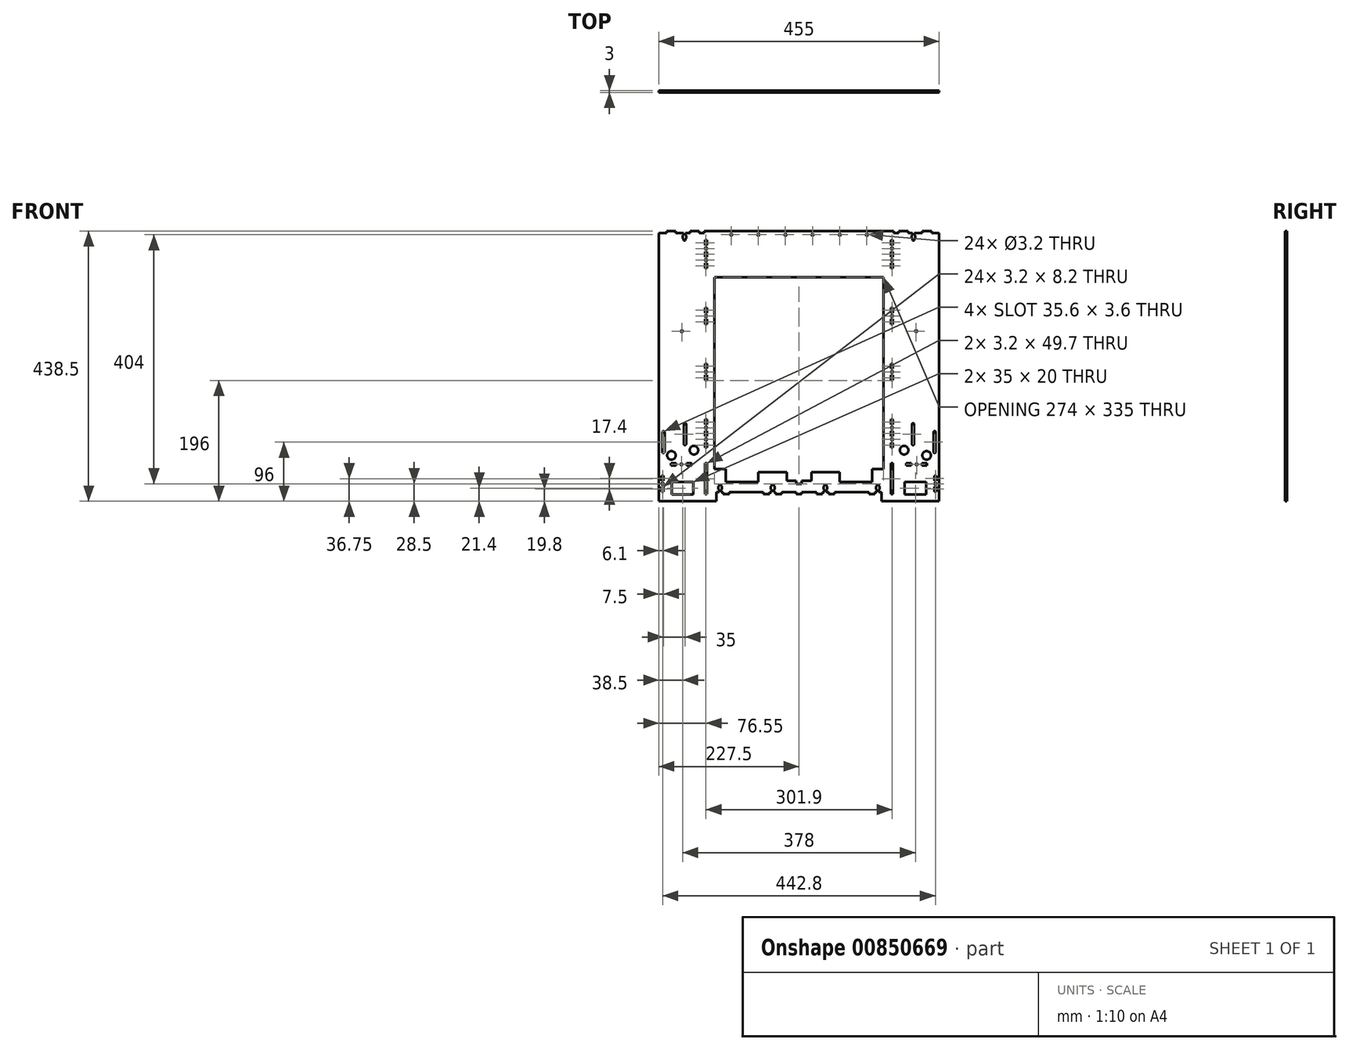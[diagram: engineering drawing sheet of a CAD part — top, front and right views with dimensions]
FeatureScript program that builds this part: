
annotation { "Feature Type Name" : "Feature", "Feature Type Description" : "" }
export const myFeature = defineFeature(function(context is Context, id is Id, definition is map)
    precondition{}
    {
        {
            var Q0;
            Q0=qCreatedBy(makeId("Front.planeOp"),FACE);
            var sketch = newSketch(context, id + "F0", { "sketchPlane" : qUnion([Q0])});
            skLineSegment(sketch, "E0", {"start": v(0, 0) * mm, "end": v(0, 435.5) * mm});
            skLineSegment(sketch, "E1", {"start": v(0, 435.5) * mm, "end": v(12.5, 435.5) * mm});
            skLineSegment(sketch, "E2", {"start": v(12.5, 435.5) * mm, "end": v(12.5, 438.5) * mm});
            skLineSegment(sketch, "E3", {"start": v(12.5, 438.5) * mm, "end": v(27.5, 438.5) * mm});
            skLineSegment(sketch, "E4", {"start": v(27.5, 438.5) * mm, "end": v(27.5, 435.5) * mm});
            skLineSegment(sketch, "E5", {"start": v(27.5, 435.5) * mm, "end": v(40, 435.5) * mm});
            skLineSegment(sketch, "E6", {"start": v(40, 435.5) * mm, "end": v(40, 431.2) * mm});
            skLineSegment(sketch, "E7", {"start": v(40, 431.2) * mm, "end": v(38.75, 431.2) * mm});
            skLineSegment(sketch, "E8", {"start": v(38.75, 431.2) * mm, "end": v(38.75, 426.2) * mm});
            skLineSegment(sketch, "E9", {"start": v(38.75, 426.2) * mm, "end": v(40, 426.2) * mm});
            skLineSegment(sketch, "E10", {"start": v(40, 426.2) * mm, "end": v(40, 423.5) * mm});
            skLineSegment(sketch, "E11", {"start": v(40, 423.5) * mm, "end": v(43.5, 423.5) * mm});
            skLineSegment(sketch, "E12", {"start": v(43.5, 423.5) * mm, "end": v(43.5, 426.2) * mm});
            skLineSegment(sketch, "E13", {"start": v(43.5, 426.2) * mm, "end": v(44.75, 426.2) * mm});
            skLineSegment(sketch, "E14", {"start": v(44.75, 426.2) * mm, "end": v(44.75, 431.2) * mm});
            skLineSegment(sketch, "E15", {"start": v(44.75, 431.2) * mm, "end": v(43.5, 431.2) * mm});
            skLineSegment(sketch, "E16", {"start": v(43.5, 431.2) * mm, "end": v(43.5, 435.5) * mm});
            skLineSegment(sketch, "E17", {"start": v(43.5, 435.5) * mm, "end": v(50.7, 435.5) * mm});
            skLineSegment(sketch, "E18", {"start": v(50.7, 435.5) * mm, "end": v(50.7, 438.5) * mm});
            skLineSegment(sketch, "E19", {"start": v(50.7, 438.5) * mm, "end": v(65.7, 438.5) * mm});
            skLineSegment(sketch, "E20", {"start": v(65.7, 438.5) * mm, "end": v(65.7, 435.5) * mm});
            skLineSegment(sketch, "E21", {"start": v(65.7, 435.5) * mm, "end": v(73.9, 435.5) * mm});
            skLineSegment(sketch, "E22", {"start": v(73.9, 435.5) * mm, "end": v(73.9, 438.5) * mm});
            skLineSegment(sketch, "E23", {"start": v(73.9, 438.5) * mm, "end": v(227.5, 438.5) * mm});
            skLineSegment(sketch, "E24", {"start": v(0, 0) * mm, "end": v(93.35, 0) * mm});
            skLineSegment(sketch, "E25", {"start": v(93.35, 0) * mm, "end": v(93.35, 15) * mm});
            skLineSegment(sketch, "E26", {"start": v(93.35, 15) * mm, "end": v(97.75, 15) * mm});
            skLineSegment(sketch, "E27", {"start": v(97.75, 15) * mm, "end": v(97.75, 19.3) * mm});
            skLineSegment(sketch, "E28", {"start": v(97.75, 19.3) * mm, "end": v(96.5, 19.3) * mm});
            skLineSegment(sketch, "E29", {"start": v(96.5, 19.3) * mm, "end": v(96.5, 24.3) * mm});
            skLineSegment(sketch, "E30", {"start": v(96.5, 24.3) * mm, "end": v(97.75, 24.3) * mm});
            skLineSegment(sketch, "E31", {"start": v(97.75, 24.3) * mm, "end": v(97.75, 27) * mm});
            skLineSegment(sketch, "E32", {"start": v(97.75, 27) * mm, "end": v(101.25, 27) * mm});
            skLineSegment(sketch, "E33", {"start": v(101.25, 27) * mm, "end": v(101.25, 24.3) * mm});
            skLineSegment(sketch, "E34", {"start": v(101.25, 24.3) * mm, "end": v(102.5, 24.3) * mm});
            skLineSegment(sketch, "E35", {"start": v(102.5, 24.3) * mm, "end": v(102.5, 19.3) * mm});
            skLineSegment(sketch, "E36", {"start": v(102.5, 19.3) * mm, "end": v(101.25, 19.3) * mm});
            skLineSegment(sketch, "E37", {"start": v(101.25, 19.3) * mm, "end": v(101.25, 15) * mm});
            skLineSegment(sketch, "E38", {"start": v(101.25, 15) * mm, "end": v(104.35, 15) * mm});
            skLineSegment(sketch, "E39", {"start": v(104.35, 15) * mm, "end": v(104.35, 12) * mm});
            skLineSegment(sketch, "E40", {"start": v(104.35, 12) * mm, "end": v(114.15, 12) * mm});
            skLineSegment(sketch, "E41", {"start": v(114.15, 12) * mm, "end": v(114.15, 15) * mm});
            skLineSegment(sketch, "E42", {"start": v(114.15, 15) * mm, "end": v(169.85, 15) * mm});
            skLineSegment(sketch, "E43", {"start": v(169.85, 15) * mm, "end": v(169.85, 12) * mm});
            skLineSegment(sketch, "E44", {"start": v(169.85, 12) * mm, "end": v(179.65, 12) * mm});
            skLineSegment(sketch, "E45", {"start": v(179.65, 12) * mm, "end": v(179.65, 15) * mm});
            skLineSegment(sketch, "E46", {"start": v(179.65, 15) * mm, "end": v(183.05, 15) * mm});
            skLineSegment(sketch, "E47", {"start": v(183.05, 15) * mm, "end": v(183.05, 19.3) * mm});
            skLineSegment(sketch, "E48", {"start": v(183.05, 19.3) * mm, "end": v(181.8, 19.3) * mm});
            skLineSegment(sketch, "E49", {"start": v(181.8, 19.3) * mm, "end": v(181.8, 24.3) * mm});
            skLineSegment(sketch, "E50", {"start": v(181.8, 24.3) * mm, "end": v(183.05, 24.3) * mm});
            skLineSegment(sketch, "E51", {"start": v(183.05, 24.3) * mm, "end": v(183.05, 27) * mm});
            skLineSegment(sketch, "E52", {"start": v(183.05, 27) * mm, "end": v(186.55, 27) * mm});
            skLineSegment(sketch, "E53", {"start": v(186.55, 27) * mm, "end": v(186.55, 24.3) * mm});
            skLineSegment(sketch, "E54", {"start": v(186.55, 24.3) * mm, "end": v(187.8, 24.3) * mm});
            skLineSegment(sketch, "E55", {"start": v(187.8, 24.3) * mm, "end": v(187.8, 19.3) * mm});
            skLineSegment(sketch, "E56", {"start": v(187.8, 19.3) * mm, "end": v(186.55, 19.3) * mm});
            skLineSegment(sketch, "E57", {"start": v(186.55, 19.3) * mm, "end": v(186.55, 15) * mm});
            skLineSegment(sketch, "E58", {"start": v(186.55, 15) * mm, "end": v(189.35, 15) * mm});
            skLineSegment(sketch, "E59", {"start": v(189.35, 15) * mm, "end": v(189.35, 12) * mm});
            skLineSegment(sketch, "E60", {"start": v(189.35, 12) * mm, "end": v(199.15, 12) * mm});
            skLineSegment(sketch, "E61", {"start": v(199.15, 12) * mm, "end": v(199.15, 15) * mm});
            skLineSegment(sketch, "E62", {"start": v(199.15, 15) * mm, "end": v(223, 15) * mm});
            skLineSegment(sketch, "E63", {"start": v(223, 15) * mm, "end": v(223, 12) * mm});
            skLineSegment(sketch, "E64", {"start": v(223, 12) * mm, "end": v(227.5, 12) * mm});
            skLineSegment(sketch, "E65", {"start": v(227.5, 12) * mm, "end": v(227.5, 438.5) * mm, "construction": true});
            skLineSegment(sketch, "E66", {"start": v(227.5, 28.5) * mm, "end": v(223, 28.5) * mm});
            skLineSegment(sketch, "E67", {"start": v(223, 28.5) * mm, "end": v(223, 33.5) * mm});
            skLineSegment(sketch, "E68", {"start": v(223, 33.5) * mm, "end": v(207.5, 33.5) * mm});
            skLineSegment(sketch, "E69", {"start": v(207.5, 33.5) * mm, "end": v(207.5, 47.5) * mm});
            skLineSegment(sketch, "E70", {"start": v(207.5, 47.5) * mm, "end": v(161.5, 47.5) * mm});
            skLineSegment(sketch, "E71", {"start": v(161.5, 47.5) * mm, "end": v(161.5, 31.5) * mm});
            skLineSegment(sketch, "E72", {"start": v(161.5, 31.5) * mm, "end": v(108.6, 31.5) * mm});
            skLineSegment(sketch, "E73", {"start": v(108.6, 31.5) * mm, "end": v(108.6, 52.5) * mm});
            skLineSegment(sketch, "E74", {"start": v(227.5, 363.5) * mm, "end": v(90.5, 363.5) * mm});
            skLineSegment(sketch, "E75", {"start": v(108.6, 52.5) * mm, "end": v(90.5, 52.5) * mm});
            skLineSegment(sketch, "E76", {"start": v(90.5, 363.5) * mm, "end": v(90.5, 52.5) * mm});
            skCircle(sketch, "E77", {"center": v(117.5, 432.5) * mm, "radius": 1.6 * mm});
            skCircle(sketch, "E78.1.0.0", {"center": v(161.5, 432.5) * mm, "radius": 1.6 * mm});
            skCircle(sketch, "E78.2.0.0", {"center": v(205.5, 432.5) * mm, "radius": 1.6 * mm});
            skLineSegment(sketch, "E78.direction1", {"start": v(117.5, 432.5) * mm, "end": v(161.5, 432.5) * mm, "construction": true});
            skLineSegment(sketch, "E79.MirrorCS", {"start": v(268.45, 24.3) * mm, "end": v(267.2, 24.3) * mm});
            skLineSegment(sketch, "E80.MirrorCS", {"start": v(411.5, 423.5) * mm, "end": v(411.5, 426.2) * mm});
            skLineSegment(sketch, "E81.MirrorCS", {"start": v(353.75, 24.3) * mm, "end": v(352.5, 24.3) * mm});
            skLineSegment(sketch, "E82.MirrorCS", {"start": v(271.95, 24.3) * mm, "end": v(271.95, 27) * mm});
            skLineSegment(sketch, "E83.MirrorCS", {"start": v(275.35, 15) * mm, "end": v(271.95, 15) * mm});
            skLineSegment(sketch, "E84.MirrorCS", {"start": v(353.75, 15) * mm, "end": v(350.65, 15) * mm});
            skLineSegment(sketch, "E85.MirrorCS", {"start": v(410.25, 431.2) * mm, "end": v(411.5, 431.2) * mm});
            skLineSegment(sketch, "E86.MirrorCS", {"start": v(411.5, 426.2) * mm, "end": v(410.25, 426.2) * mm});
            skLineSegment(sketch, "E87.MirrorCS", {"start": v(352.5, 19.3) * mm, "end": v(353.75, 19.3) * mm});
            skLineSegment(sketch, "E88.MirrorCS", {"start": v(357.25, 24.3) * mm, "end": v(357.25, 27) * mm});
            skLineSegment(sketch, "E89.MirrorCS", {"start": v(273.2, 24.3) * mm, "end": v(271.95, 24.3) * mm});
            skLineSegment(sketch, "E90.MirrorCS", {"start": v(353.75, 27) * mm, "end": v(353.75, 24.3) * mm});
            skLineSegment(sketch, "E91.MirrorCS", {"start": v(268.45, 27) * mm, "end": v(268.45, 24.3) * mm});
            skLineSegment(sketch, "E92.MirrorCS", {"start": v(415, 426.2) * mm, "end": v(415, 423.5) * mm});
            skLineSegment(sketch, "E93.MirrorCS", {"start": v(358.5, 24.3) * mm, "end": v(357.25, 24.3) * mm});
            skLineSegment(sketch, "E94.MirrorCS", {"start": v(267.2, 19.3) * mm, "end": v(268.45, 19.3) * mm});
            skLineSegment(sketch, "E95.MirrorCS", {"start": v(357.25, 19.3) * mm, "end": v(358.5, 19.3) * mm});
            skLineSegment(sketch, "E96.MirrorCS", {"start": v(410.25, 426.2) * mm, "end": v(410.25, 431.2) * mm});
            skLineSegment(sketch, "E97.MirrorCS", {"start": v(273.2, 19.3) * mm, "end": v(273.2, 24.3) * mm});
            skLineSegment(sketch, "E98.MirrorCS", {"start": v(268.45, 15) * mm, "end": v(265.65, 15) * mm});
            skLineSegment(sketch, "E99.MirrorCS", {"start": v(271.95, 27) * mm, "end": v(268.45, 27) * mm});
            skLineSegment(sketch, "E100.MirrorCS", {"start": v(415, 435.5) * mm, "end": v(415, 431.2) * mm});
            skLineSegment(sketch, "E101.MirrorCS", {"start": v(265.65, 15) * mm, "end": v(265.65, 12) * mm});
            skLineSegment(sketch, "E102.MirrorCS", {"start": v(267.2, 24.3) * mm, "end": v(267.2, 19.3) * mm});
            skLineSegment(sketch, "E103.MirrorCS", {"start": v(271.95, 15) * mm, "end": v(271.95, 19.3) * mm});
            skLineSegment(sketch, "E104.MirrorCS", {"start": v(415, 431.2) * mm, "end": v(416.25, 431.2) * mm});
            skLineSegment(sketch, "E105.MirrorCS", {"start": v(404.3, 435.5) * mm, "end": v(404.3, 438.5) * mm});
            skLineSegment(sketch, "E106.MirrorCS", {"start": v(416.25, 431.2) * mm, "end": v(416.25, 426.2) * mm});
            skLineSegment(sketch, "E107.MirrorCS", {"start": v(350.65, 15) * mm, "end": v(350.65, 12) * mm});
            skLineSegment(sketch, "E108.MirrorCS", {"start": v(268.45, 19.3) * mm, "end": v(268.45, 15) * mm});
            skLineSegment(sketch, "E109.MirrorCS", {"start": v(271.95, 19.3) * mm, "end": v(273.2, 19.3) * mm});
            skLineSegment(sketch, "E110.MirrorCS", {"start": v(411.5, 435.5) * mm, "end": v(404.3, 435.5) * mm});
            skLineSegment(sketch, "E111.MirrorCS", {"start": v(361.65, 15) * mm, "end": v(357.25, 15) * mm});
            skLineSegment(sketch, "E112.MirrorCS", {"start": v(416.25, 426.2) * mm, "end": v(415, 426.2) * mm});
            skLineSegment(sketch, "E113.MirrorCS", {"start": v(427.5, 435.5) * mm, "end": v(415, 435.5) * mm});
            skLineSegment(sketch, "E114.MirrorCS", {"start": v(353.75, 19.3) * mm, "end": v(353.75, 15) * mm});
            skLineSegment(sketch, "E115.MirrorCS", {"start": v(357.25, 15) * mm, "end": v(357.25, 19.3) * mm});
            skLineSegment(sketch, "E116.MirrorCS", {"start": v(358.5, 19.3) * mm, "end": v(358.5, 24.3) * mm});
            skLineSegment(sketch, "E117.MirrorCS", {"start": v(415, 423.5) * mm, "end": v(411.5, 423.5) * mm});
            skLineSegment(sketch, "E118.MirrorCS", {"start": v(357.25, 27) * mm, "end": v(353.75, 27) * mm});
            skLineSegment(sketch, "E119.MirrorCS", {"start": v(352.5, 24.3) * mm, "end": v(352.5, 19.3) * mm});
            skLineSegment(sketch, "E120.MirrorCS", {"start": v(275.35, 12) * mm, "end": v(275.35, 15) * mm});
            skLineSegment(sketch, "E121.MirrorCS", {"start": v(411.5, 431.2) * mm, "end": v(411.5, 435.5) * mm});
            skLineSegment(sketch, "E122.MirrorCS", {"start": v(265.65, 12) * mm, "end": v(255.85, 12) * mm});
            skLineSegment(sketch, "E123.MirrorCS", {"start": v(389.3, 438.5) * mm, "end": v(389.3, 435.5) * mm});
            skLineSegment(sketch, "E124.MirrorCS", {"start": v(285.15, 12) * mm, "end": v(275.35, 12) * mm});
            skLineSegment(sketch, "E125.MirrorCS", {"start": v(381.1, 435.5) * mm, "end": v(381.1, 438.5) * mm});
            skLineSegment(sketch, "E126.MirrorCS", {"start": v(232, 12) * mm, "end": v(227.5, 12) * mm});
            skLineSegment(sketch, "E127.MirrorCS", {"start": v(232, 15) * mm, "end": v(232, 12) * mm});
            skLineSegment(sketch, "E128.MirrorCS", {"start": v(232, 28.5) * mm, "end": v(232, 33.5) * mm});
            skLineSegment(sketch, "E129.MirrorCS", {"start": v(442.5, 435.5) * mm, "end": v(442.5, 438.5) * mm});
            skLineSegment(sketch, "E130.MirrorCS", {"start": v(404.3, 438.5) * mm, "end": v(389.3, 438.5) * mm});
            skLineSegment(sketch, "E131.MirrorCS", {"start": v(255.85, 12) * mm, "end": v(255.85, 15) * mm});
            skLineSegment(sketch, "E132.MirrorCS", {"start": v(350.65, 12) * mm, "end": v(340.85, 12) * mm});
            skLineSegment(sketch, "E133.MirrorCS", {"start": v(427.5, 438.5) * mm, "end": v(427.5, 435.5) * mm});
            skLineSegment(sketch, "E134.MirrorCS", {"start": v(255.85, 15) * mm, "end": v(232, 15) * mm});
            skLineSegment(sketch, "E135.MirrorCS", {"start": v(340.85, 12) * mm, "end": v(340.85, 15) * mm});
            skLineSegment(sketch, "E136.MirrorCS", {"start": v(232, 33.5) * mm, "end": v(247.5, 33.5) * mm});
            skLineSegment(sketch, "E137.MirrorCS", {"start": v(285.15, 15) * mm, "end": v(285.15, 12) * mm});
            skLineSegment(sketch, "E138.MirrorCS", {"start": v(389.3, 435.5) * mm, "end": v(381.1, 435.5) * mm});
            skLineSegment(sketch, "E139.MirrorCS", {"start": v(227.5, 28.5) * mm, "end": v(232, 28.5) * mm});
            skLineSegment(sketch, "E140.MirrorCS", {"start": v(247.5, 33.5) * mm, "end": v(247.5, 47.5) * mm});
            skLineSegment(sketch, "E141.MirrorCS", {"start": v(346.4, 31.5) * mm, "end": v(346.4, 52.5) * mm});
            skLineSegment(sketch, "E142.MirrorCS", {"start": v(346.4, 52.5) * mm, "end": v(364.5, 52.5) * mm});
            skLineSegment(sketch, "E143.MirrorCS", {"start": v(455, 435.5) * mm, "end": v(442.5, 435.5) * mm});
            skLineSegment(sketch, "E144.MirrorCS", {"start": v(442.5, 438.5) * mm, "end": v(427.5, 438.5) * mm});
            skLineSegment(sketch, "E145.MirrorCS", {"start": v(361.65, 0) * mm, "end": v(361.65, 15) * mm});
            skCircle(sketch, "E146.MirrorC", {"center": v(293.5, 432.5) * mm, "radius": 1.6 * mm});
            skLineSegment(sketch, "E147.MirrorCS", {"start": v(293.5, 47.5) * mm, "end": v(293.5, 31.5) * mm});
            skCircle(sketch, "E148.MirrorC", {"center": v(337.5, 432.5) * mm, "radius": 1.6 * mm});
            skCircle(sketch, "E149.MirrorC", {"center": v(249.5, 432.5) * mm, "radius": 1.6 * mm});
            skLineSegment(sketch, "E150.MirrorCS", {"start": v(293.5, 31.5) * mm, "end": v(346.4, 31.5) * mm});
            skLineSegment(sketch, "E151.MirrorCS", {"start": v(340.85, 15) * mm, "end": v(285.15, 15) * mm});
            skLineSegment(sketch, "E152.MirrorCS", {"start": v(247.5, 47.5) * mm, "end": v(293.5, 47.5) * mm});
            skLineSegment(sketch, "E153.MirrorCS", {"start": v(337.5, 432.5) * mm, "end": v(293.5, 432.5) * mm, "construction": true});
            skLineSegment(sketch, "E154.MirrorCS", {"start": v(381.1, 438.5) * mm, "end": v(227.5, 438.5) * mm});
            skLineSegment(sketch, "E155.MirrorCS", {"start": v(364.5, 363.5) * mm, "end": v(364.5, 52.5) * mm});
            skLineSegment(sketch, "E156.MirrorCS", {"start": v(227.5, 363.5) * mm, "end": v(364.5, 363.5) * mm});
            skLineSegment(sketch, "E157.MirrorCS", {"start": v(455, 0) * mm, "end": v(455, 435.5) * mm});
            skLineSegment(sketch, "E158.MirrorCS", {"start": v(455, 0) * mm, "end": v(361.65, 0) * mm});
            skLineSegment(sketch, "E159.bottom", {"start": v(21, 31.4) * mm, "end": v(56, 31.4) * mm});
            skLineSegment(sketch, "E159.top", {"start": v(21, 11.4) * mm, "end": v(56, 11.4) * mm});
            skLineSegment(sketch, "E159.left", {"start": v(21, 31.4) * mm, "end": v(21, 11.4) * mm});
            skLineSegment(sketch, "E159.right", {"start": v(56, 31.4) * mm, "end": v(56, 11.4) * mm});
            skLineSegment(sketch, "E160.bottom", {"start": v(74.95, 61.6) * mm, "end": v(78.15, 61.6) * mm});
            skLineSegment(sketch, "E160.top", {"start": v(74.95, 11.9) * mm, "end": v(78.15, 11.9) * mm});
            skLineSegment(sketch, "E160.left", {"start": v(74.95, 61.6) * mm, "end": v(74.95, 11.9) * mm});
            skLineSegment(sketch, "E160.right", {"start": v(78.15, 61.6) * mm, "end": v(78.15, 11.9) * mm});
            skLineSegment(sketch, "E161.bottom", {"start": v(4.5, 15.7) * mm, "end": v(7.7, 15.7) * mm});
            skLineSegment(sketch, "E161.top", {"start": v(4.5, 23.9) * mm, "end": v(7.7, 23.9) * mm});
            skLineSegment(sketch, "E161.left", {"start": v(4.5, 15.7) * mm, "end": v(4.5, 23.9) * mm});
            skLineSegment(sketch, "E161.right", {"start": v(7.7, 15.7) * mm, "end": v(7.7, 23.9) * mm});
            skCircle(sketch, "E162", {"center": v(6.1, 28.5) * mm, "radius": 1.6 * mm});
            skPoint(sketch, "E163", {"position": v(6.1, 23.9) * mm});
            skLineSegment(sketch, "E164", {"start": v(6.1, 28.5) * mm, "end": v(9.1, 28.5) * mm, "construction": true});
            skLineSegment(sketch, "E165.MirrorCS", {"start": v(4.5, 41.3) * mm, "end": v(7.7, 41.3) * mm});
            skLineSegment(sketch, "E166.MirrorCS", {"start": v(4.5, 41.3) * mm, "end": v(4.5, 33.1) * mm});
            skPoint(sketch, "E167.MirrorP", {"position": v(6.1, 33.1) * mm});
            skLineSegment(sketch, "E168.MirrorCS", {"start": v(7.7, 41.3) * mm, "end": v(7.7, 33.1) * mm});
            skLineSegment(sketch, "E169.MirrorCS", {"start": v(4.5, 33.1) * mm, "end": v(7.7, 33.1) * mm});
            skLineSegment(sketch, "E170.bottom", {"start": v(19.8, 61.6) * mm, "end": v(28, 61.6) * mm});
            skLineSegment(sketch, "E170.top", {"start": v(19.8, 58.4) * mm, "end": v(28, 58.4) * mm});
            skLineSegment(sketch, "E170.left", {"start": v(19.8, 61.6) * mm, "end": v(19.8, 58.4) * mm});
            skLineSegment(sketch, "E170.right", {"start": v(28, 61.6) * mm, "end": v(28, 58.4) * mm});
            skPoint(sketch, "E171", {"position": v(28, 60) * mm});
            skCircle(sketch, "E172", {"center": v(36.7, 60) * mm, "radius": 1.6 * mm});
            skLineSegment(sketch, "E173", {"start": v(36.7, 60) * mm, "end": v(36.7, 61.6) * mm, "construction": true});
            skLineSegment(sketch, "E174.MirrorCS", {"start": v(53.6, 58.4) * mm, "end": v(45.4, 58.4) * mm});
            skLineSegment(sketch, "E175.MirrorCS", {"start": v(45.4, 61.6) * mm, "end": v(45.4, 58.4) * mm});
            skPoint(sketch, "E176.MirrorP", {"position": v(45.4, 60) * mm});
            skLineSegment(sketch, "E177.MirrorCS", {"start": v(53.6, 61.6) * mm, "end": v(53.6, 58.4) * mm});
            skLineSegment(sketch, "E178.MirrorCS", {"start": v(53.6, 61.6) * mm, "end": v(45.4, 61.6) * mm});
            skLineSegment(sketch, "E179.bottom", {"start": v(78.15, 87) * mm, "end": v(74.95, 87) * mm});
            skLineSegment(sketch, "E179.top", {"start": v(78.15, 95.2) * mm, "end": v(74.95, 95.2) * mm});
            skLineSegment(sketch, "E179.left", {"start": v(78.15, 87) * mm, "end": v(78.15, 95.2) * mm});
            skLineSegment(sketch, "E179.right", {"start": v(74.95, 87) * mm, "end": v(74.95, 95.2) * mm});
            skCircle(sketch, "E180", {"center": v(76.55, 100.5) * mm, "radius": 1.6 * mm});
            skPoint(sketch, "E180.centerSnap0", {"position": v(76.55, 95.2) * mm});
            skLineSegment(sketch, "E181", {"start": v(76.55, 100.5) * mm, "end": v(78.15, 100.5) * mm, "construction": true});
            skLineSegment(sketch, "E182.MirrorCS", {"start": v(78.15, 105.8) * mm, "end": v(74.95, 105.8) * mm});
            skLineSegment(sketch, "E183.MirrorCS", {"start": v(78.15, 114) * mm, "end": v(74.95, 114) * mm});
            skLineSegment(sketch, "E184.MirrorCS", {"start": v(78.15, 114) * mm, "end": v(78.15, 105.8) * mm});
            skLineSegment(sketch, "E185.MirrorCS", {"start": v(74.95, 114) * mm, "end": v(74.95, 105.8) * mm});
            skPoint(sketch, "E186.MirrorP", {"position": v(76.55, 105.8) * mm});
            skCircle(sketch, "E187.0.1.0", {"center": v(76.55, 119.3) * mm, "radius": 1.6 * mm});
            skLineSegment(sketch, "E187.direction1", {"start": v(76.55, 100.5) * mm, "end": v(101.55, 100.5) * mm, "construction": true});
            skLineSegment(sketch, "E187.direction2", {"start": v(76.55, 100.5) * mm, "end": v(76.55, 119.3) * mm, "construction": true});
            skLineSegment(sketch, "E188", {"start": v(76.55, 119.3) * mm, "end": v(78.15, 119.3) * mm, "construction": true});
            skLineSegment(sketch, "E189.MirrorCS", {"start": v(78.15, 132.8) * mm, "end": v(74.95, 132.8) * mm});
            skPoint(sketch, "E190.MirrorP", {"position": v(76.55, 132.8) * mm});
            skLineSegment(sketch, "E191.MirrorCS", {"start": v(78.15, 124.6) * mm, "end": v(74.95, 124.6) * mm});
            skLineSegment(sketch, "E192.MirrorCS", {"start": v(78.15, 124.6) * mm, "end": v(78.15, 132.8) * mm});
            skLineSegment(sketch, "E193.MirrorCS", {"start": v(74.95, 124.6) * mm, "end": v(74.95, 132.8) * mm});
            skLineSegment(sketch, "E194.0.1.3", {"start": v(74.95, 223.5) * mm, "end": v(74.95, 215.3) * mm});
            skLineSegment(sketch, "E194.0.1.5", {"start": v(74.95, 196.5) * mm, "end": v(74.95, 204.7) * mm});
            skLineSegment(sketch, "E194.0.1.6", {"start": v(78.15, 223.5) * mm, "end": v(78.15, 215.3) * mm});
            skPoint(sketch, "E194.0.1.7", {"position": v(76.55, 204.7) * mm});
            skCircle(sketch, "E194.0.1.8", {"center": v(76.55, 210) * mm, "radius": 1.6 * mm});
            skLineSegment(sketch, "E194.0.1.9", {"start": v(78.15, 196.5) * mm, "end": v(78.15, 204.7) * mm});
            skLineSegment(sketch, "E194.0.1.10", {"start": v(76.55, 210) * mm, "end": v(76.55, 228.8) * mm, "construction": true});
            skPoint(sketch, "E194.0.1.11", {"position": v(76.55, 215.3) * mm});
            skLineSegment(sketch, "E194.0.1.14", {"start": v(78.15, 215.3) * mm, "end": v(74.95, 215.3) * mm});
            skLineSegment(sketch, "E194.0.1.15", {"start": v(78.15, 223.5) * mm, "end": v(74.95, 223.5) * mm});
            skLineSegment(sketch, "E194.0.1.16", {"start": v(78.15, 204.7) * mm, "end": v(74.95, 204.7) * mm});
            skLineSegment(sketch, "E194.0.1.17", {"start": v(78.15, 196.5) * mm, "end": v(74.95, 196.5) * mm});
            skLineSegment(sketch, "E194.0.1.19", {"start": v(76.55, 210) * mm, "end": v(78.15, 210) * mm, "construction": true});
            skLineSegment(sketch, "E194.direction1", {"start": v(74.95, 87) * mm, "end": v(99.95, 87) * mm, "construction": true});
            skLineSegment(sketch, "E194.direction2", {"start": v(74.95, 87) * mm, "end": v(74.95, 196.5) * mm, "construction": true});
            skCircle(sketch, "E195.0.1.0", {"center": v(76.55, 300.7) * mm, "radius": 1.6 * mm});
            skPoint(sketch, "E195.0.1.2", {"position": v(76.55, 295.4) * mm});
            skLineSegment(sketch, "E195.0.1.4", {"start": v(74.95, 287.2) * mm, "end": v(74.95, 295.4) * mm});
            skPoint(sketch, "E195.0.1.6", {"position": v(76.55, 306) * mm});
            skLineSegment(sketch, "E195.0.1.7", {"start": v(78.15, 314.2) * mm, "end": v(78.15, 306) * mm});
            skLineSegment(sketch, "E195.0.1.10", {"start": v(78.15, 287.2) * mm, "end": v(78.15, 295.4) * mm});
            skLineSegment(sketch, "E195.0.1.11", {"start": v(76.55, 300.7) * mm, "end": v(76.55, 319.5) * mm, "construction": true});
            skLineSegment(sketch, "E195.0.1.12", {"start": v(78.15, 314.2) * mm, "end": v(74.95, 314.2) * mm});
            skLineSegment(sketch, "E195.0.1.13", {"start": v(74.95, 314.2) * mm, "end": v(74.95, 306) * mm});
            skLineSegment(sketch, "E195.0.1.14", {"start": v(78.15, 287.2) * mm, "end": v(74.95, 287.2) * mm});
            skLineSegment(sketch, "E195.0.1.15", {"start": v(78.15, 295.4) * mm, "end": v(74.95, 295.4) * mm});
            skLineSegment(sketch, "E195.0.1.18", {"start": v(76.55, 300.7) * mm, "end": v(78.15, 300.7) * mm, "construction": true});
            skLineSegment(sketch, "E195.0.1.19", {"start": v(78.15, 306) * mm, "end": v(74.95, 306) * mm});
            skCircle(sketch, "E195.0.2.0", {"center": v(76.55, 391.4) * mm, "radius": 1.6 * mm});
            skLineSegment(sketch, "E195.0.2.1", {"start": v(78.15, 415.5) * mm, "end": v(78.15, 423.7) * mm});
            skPoint(sketch, "E195.0.2.2", {"position": v(76.55, 386.1) * mm});
            skCircle(sketch, "E195.0.2.3", {"center": v(76.55, 410.2) * mm, "radius": 1.6 * mm});
            skLineSegment(sketch, "E195.0.2.4", {"start": v(74.95, 377.9) * mm, "end": v(74.95, 386.1) * mm});
            skPoint(sketch, "E195.0.2.5", {"position": v(76.55, 423.7) * mm});
            skPoint(sketch, "E195.0.2.6", {"position": v(76.55, 396.7) * mm});
            skLineSegment(sketch, "E195.0.2.7", {"start": v(78.15, 404.9) * mm, "end": v(78.15, 396.7) * mm});
            skLineSegment(sketch, "E195.0.2.8", {"start": v(74.95, 415.5) * mm, "end": v(74.95, 423.7) * mm});
            skLineSegment(sketch, "E195.0.2.9", {"start": v(78.15, 415.5) * mm, "end": v(74.95, 415.5) * mm});
            skLineSegment(sketch, "E195.0.2.10", {"start": v(78.15, 377.9) * mm, "end": v(78.15, 386.1) * mm});
            skLineSegment(sketch, "E195.0.2.11", {"start": v(76.55, 391.4) * mm, "end": v(76.55, 410.2) * mm, "construction": true});
            skLineSegment(sketch, "E195.0.2.12", {"start": v(78.15, 404.9) * mm, "end": v(74.95, 404.9) * mm});
            skLineSegment(sketch, "E195.0.2.13", {"start": v(74.95, 404.9) * mm, "end": v(74.95, 396.7) * mm});
            skLineSegment(sketch, "E195.0.2.14", {"start": v(78.15, 377.9) * mm, "end": v(74.95, 377.9) * mm});
            skLineSegment(sketch, "E195.0.2.15", {"start": v(78.15, 386.1) * mm, "end": v(74.95, 386.1) * mm});
            skLineSegment(sketch, "E195.0.2.16", {"start": v(78.15, 423.7) * mm, "end": v(74.95, 423.7) * mm});
            skLineSegment(sketch, "E195.0.2.17", {"start": v(76.55, 410.2) * mm, "end": v(78.15, 410.2) * mm, "construction": true});
            skLineSegment(sketch, "E195.0.2.18", {"start": v(76.55, 391.4) * mm, "end": v(78.15, 391.4) * mm, "construction": true});
            skLineSegment(sketch, "E195.0.2.19", {"start": v(78.15, 396.7) * mm, "end": v(74.95, 396.7) * mm});
            skLineSegment(sketch, "E195.direction1", {"start": v(74.95, 196.5) * mm, "end": v(88.43, 196.5) * mm, "construction": true});
            skLineSegment(sketch, "E195.direction2", {"start": v(74.95, 196.5) * mm, "end": v(74.95, 287.2) * mm, "construction": true});
            skCircle(sketch, "E196", {"center": v(20.5, 74.5) * mm, "radius": 7 * mm});
            skCircle(sketch, "E197", {"center": v(57, 83) * mm, "radius": 7 * mm});
            skLineSegment(sketch, "E198.left", {"start": v(5.7, 112) * mm, "end": v(5.7, 80) * mm});
            skLineSegment(sketch, "E198.right", {"start": v(9.3, 112) * mm, "end": v(9.3, 80) * mm});
            skArc(sketch, "E199", {"start": v(9.3, 112) * mm, "mid": v(7.5, 113.8) * mm, "end": v(5.7, 112) * mm});
            skArc(sketch, "E200", {"start": v(5.7, 80) * mm, "mid": v(7.5, 78.2) * mm, "end": v(9.3, 80) * mm});
            skLineSegment(sketch, "E201.left", {"start": v(40.7, 125) * mm, "end": v(40.7, 93) * mm});
            skLineSegment(sketch, "E201.right", {"start": v(44.3, 125) * mm, "end": v(44.3, 93) * mm});
            skArc(sketch, "E202", {"start": v(44.3, 125) * mm, "mid": v(42.5, 126.8) * mm, "end": v(40.7, 125) * mm});
            skArc(sketch, "E203", {"start": v(40.7, 93) * mm, "mid": v(42.5, 91.2) * mm, "end": v(44.3, 93) * mm});
            skCircle(sketch, "E204", {"center": v(37.45, 276) * mm, "radius": 1.6 * mm});
            skLineSegment(sketch, "E205.MirrorCS", {"start": v(380.05, 61.6) * mm, "end": v(380.05, 11.9) * mm});
            skLineSegment(sketch, "E206.MirrorCS", {"start": v(376.85, 61.6) * mm, "end": v(376.85, 11.9) * mm});
            skLineSegment(sketch, "E207.MirrorCS", {"start": v(450.5, 23.9) * mm, "end": v(447.3, 23.9) * mm});
            skLineSegment(sketch, "E208.MirrorCS", {"start": v(450.5, 15.7) * mm, "end": v(447.3, 15.7) * mm});
            skCircle(sketch, "E209.MirrorC", {"center": v(448.9, 28.5) * mm, "radius": 1.6 * mm});
            skLineSegment(sketch, "E210.MirrorCS", {"start": v(380.05, 11.9) * mm, "end": v(376.85, 11.9) * mm});
            skLineSegment(sketch, "E211.MirrorCS", {"start": v(450.5, 41.3) * mm, "end": v(447.3, 41.3) * mm});
            skLineSegment(sketch, "E212.MirrorCS", {"start": v(450.5, 33.1) * mm, "end": v(447.3, 33.1) * mm});
            skLineSegment(sketch, "E213.MirrorCS", {"start": v(448.9, 28.5) * mm, "end": v(445.9, 28.5) * mm, "construction": true});
            skLineSegment(sketch, "E214.MirrorCS", {"start": v(447.3, 15.7) * mm, "end": v(447.3, 23.9) * mm});
            skLineSegment(sketch, "E215.MirrorCS", {"start": v(450.5, 41.3) * mm, "end": v(450.5, 33.1) * mm});
            skLineSegment(sketch, "E216.MirrorCS", {"start": v(434, 31.4) * mm, "end": v(399, 31.4) * mm});
            skPoint(sketch, "E217.MirrorP", {"position": v(448.9, 33.1) * mm});
            skLineSegment(sketch, "E218.MirrorCS", {"start": v(450.5, 15.7) * mm, "end": v(450.5, 23.9) * mm});
            skLineSegment(sketch, "E219.MirrorCS", {"start": v(447.3, 41.3) * mm, "end": v(447.3, 33.1) * mm});
            skPoint(sketch, "E220.MirrorP", {"position": v(448.9, 23.9) * mm});
            skLineSegment(sketch, "E221.MirrorCS", {"start": v(434, 11.4) * mm, "end": v(399, 11.4) * mm});
            skLineSegment(sketch, "E222.MirrorCS", {"start": v(399, 31.4) * mm, "end": v(399, 11.4) * mm});
            skLineSegment(sketch, "E223.MirrorCS", {"start": v(434, 31.4) * mm, "end": v(434, 11.4) * mm});
            skLineSegment(sketch, "E224.MirrorCS", {"start": v(378.45, 100.5) * mm, "end": v(376.85, 100.5) * mm, "construction": true});
            skCircle(sketch, "E225.MirrorC", {"center": v(378.45, 100.5) * mm, "radius": 1.6 * mm});
            skLineSegment(sketch, "E226.MirrorCS", {"start": v(378.45, 119.3) * mm, "end": v(376.85, 119.3) * mm, "construction": true});
            skArc(sketch, "E227.MirrorCS", {"start": v(414.3, 93) * mm, "mid": v(412.5, 91.2) * mm, "end": v(410.7, 93) * mm});
            skCircle(sketch, "E228.MirrorC", {"center": v(378.45, 119.3) * mm, "radius": 1.6 * mm});
            skArc(sketch, "E229.MirrorCS", {"start": v(410.7, 125) * mm, "mid": v(412.5, 126.8) * mm, "end": v(414.3, 125) * mm});
            skLineSegment(sketch, "E230.MirrorCS", {"start": v(376.85, 132.8) * mm, "end": v(380.05, 132.8) * mm});
            skLineSegment(sketch, "E231.MirrorCS", {"start": v(376.85, 95.2) * mm, "end": v(380.05, 95.2) * mm});
            skLineSegment(sketch, "E232.MirrorCS", {"start": v(418.3, 60) * mm, "end": v(418.3, 61.6) * mm, "construction": true});
            skLineSegment(sketch, "E233.MirrorCS", {"start": v(376.85, 124.6) * mm, "end": v(380.05, 124.6) * mm});
            skLineSegment(sketch, "E234.MirrorCS", {"start": v(435.2, 61.6) * mm, "end": v(435.2, 58.4) * mm});
            skLineSegment(sketch, "E235.MirrorCS", {"start": v(376.85, 114) * mm, "end": v(380.05, 114) * mm});
            skLineSegment(sketch, "E236.MirrorCS", {"start": v(401.4, 61.6) * mm, "end": v(401.4, 58.4) * mm});
            skLineSegment(sketch, "E237.MirrorCS", {"start": v(376.85, 105.8) * mm, "end": v(380.05, 105.8) * mm});
            skLineSegment(sketch, "E238.MirrorCS", {"start": v(376.85, 87) * mm, "end": v(380.05, 87) * mm});
            skLineSegment(sketch, "E239.MirrorCS", {"start": v(409.6, 61.6) * mm, "end": v(409.6, 58.4) * mm});
            skArc(sketch, "E240.MirrorCS", {"start": v(445.7, 112) * mm, "mid": v(447.5, 113.8) * mm, "end": v(449.3, 112) * mm});
            skLineSegment(sketch, "E241.MirrorCS", {"start": v(427, 61.6) * mm, "end": v(427, 58.4) * mm});
            skLineSegment(sketch, "E242.MirrorCS", {"start": v(380.05, 61.6) * mm, "end": v(376.85, 61.6) * mm});
            skCircle(sketch, "E243.MirrorC", {"center": v(418.3, 60) * mm, "radius": 1.6 * mm});
            skArc(sketch, "E244.MirrorCS", {"start": v(449.3, 80) * mm, "mid": v(447.5, 78.2) * mm, "end": v(445.7, 80) * mm});
            skLineSegment(sketch, "E245.MirrorCS", {"start": v(435.2, 61.6) * mm, "end": v(427, 61.6) * mm});
            skCircle(sketch, "E246.MirrorC", {"center": v(398, 83) * mm, "radius": 7 * mm});
            skPoint(sketch, "E247.MirrorP", {"position": v(427, 60) * mm});
            skLineSegment(sketch, "E248.MirrorCS", {"start": v(445.7, 112) * mm, "end": v(445.7, 80) * mm});
            skLineSegment(sketch, "E249.MirrorCS", {"start": v(378.45, 100.5) * mm, "end": v(378.45, 119.3) * mm, "construction": true});
            skLineSegment(sketch, "E250.MirrorCS", {"start": v(401.4, 61.6) * mm, "end": v(409.6, 61.6) * mm});
            skLineSegment(sketch, "E251.MirrorCS", {"start": v(376.85, 124.6) * mm, "end": v(376.85, 132.8) * mm});
            skPoint(sketch, "E252.MirrorP", {"position": v(409.6, 60) * mm});
            skLineSegment(sketch, "E253.MirrorCS", {"start": v(380.05, 87) * mm, "end": v(380.05, 95.2) * mm});
            skLineSegment(sketch, "E254.MirrorCS", {"start": v(410.7, 125) * mm, "end": v(410.7, 93) * mm});
            skLineSegment(sketch, "E255.MirrorCS", {"start": v(449.3, 112) * mm, "end": v(449.3, 80) * mm});
            skPoint(sketch, "E256.MirrorP", {"position": v(378.45, 132.8) * mm});
            skLineSegment(sketch, "E257.MirrorCS", {"start": v(376.85, 87) * mm, "end": v(376.85, 95.2) * mm});
            skLineSegment(sketch, "E258.MirrorCS", {"start": v(435.2, 58.4) * mm, "end": v(427, 58.4) * mm});
            skLineSegment(sketch, "E259.MirrorCS", {"start": v(401.4, 58.4) * mm, "end": v(409.6, 58.4) * mm});
            skLineSegment(sketch, "E260.MirrorCS", {"start": v(414.3, 125) * mm, "end": v(414.3, 93) * mm});
            skLineSegment(sketch, "E261.MirrorCS", {"start": v(376.85, 114) * mm, "end": v(376.85, 105.8) * mm});
            skLineSegment(sketch, "E262.MirrorCS", {"start": v(380.05, 114) * mm, "end": v(380.05, 105.8) * mm});
            skPoint(sketch, "E263.MirrorP", {"position": v(378.45, 105.8) * mm});
            skCircle(sketch, "E264.MirrorC", {"center": v(434.5, 74.5) * mm, "radius": 7 * mm});
            skPoint(sketch, "E265.MirrorP", {"position": v(378.45, 95.2) * mm});
            skLineSegment(sketch, "E266.MirrorCS", {"start": v(380.05, 124.6) * mm, "end": v(380.05, 132.8) * mm});
            skLineSegment(sketch, "E267.MirrorCS", {"start": v(376.85, 196.5) * mm, "end": v(380.05, 196.5) * mm});
            skCircle(sketch, "E268.MirrorC", {"center": v(378.45, 210) * mm, "radius": 1.6 * mm});
            skLineSegment(sketch, "E269.MirrorCS", {"start": v(376.85, 204.7) * mm, "end": v(380.05, 204.7) * mm});
            skLineSegment(sketch, "E270.MirrorCS", {"start": v(378.45, 210) * mm, "end": v(376.85, 210) * mm, "construction": true});
            skLineSegment(sketch, "E271.MirrorCS", {"start": v(376.85, 215.3) * mm, "end": v(380.05, 215.3) * mm});
            skLineSegment(sketch, "E272.MirrorCS", {"start": v(380.05, 196.5) * mm, "end": v(380.05, 204.7) * mm});
            skLineSegment(sketch, "E273.MirrorCS", {"start": v(380.05, 223.5) * mm, "end": v(380.05, 215.3) * mm});
            skLineSegment(sketch, "E274.MirrorCS", {"start": v(376.85, 196.5) * mm, "end": v(376.85, 204.7) * mm});
            skLineSegment(sketch, "E275.MirrorCS", {"start": v(376.85, 223.5) * mm, "end": v(376.85, 215.3) * mm});
            skLineSegment(sketch, "E276.MirrorCS", {"start": v(376.85, 223.5) * mm, "end": v(380.05, 223.5) * mm});
            skLineSegment(sketch, "E277.MirrorCS", {"start": v(378.45, 210) * mm, "end": v(378.45, 228.8) * mm, "construction": true});
            skPoint(sketch, "E278.MirrorP", {"position": v(378.45, 215.3) * mm});
            skPoint(sketch, "E279.MirrorP", {"position": v(378.45, 204.7) * mm});
            skLineSegment(sketch, "E280.MirrorCS", {"start": v(378.45, 300.7) * mm, "end": v(376.85, 300.7) * mm, "construction": true});
            skCircle(sketch, "E281.MirrorC", {"center": v(378.45, 300.7) * mm, "radius": 1.6 * mm});
            skLineSegment(sketch, "E282.MirrorCS", {"start": v(376.85, 306) * mm, "end": v(380.05, 306) * mm});
            skLineSegment(sketch, "E283.MirrorCS", {"start": v(376.85, 287.2) * mm, "end": v(380.05, 287.2) * mm});
            skLineSegment(sketch, "E284.MirrorCS", {"start": v(380.05, 287.2) * mm, "end": v(380.05, 295.4) * mm});
            skLineSegment(sketch, "E285.MirrorCS", {"start": v(376.85, 295.4) * mm, "end": v(380.05, 295.4) * mm});
            skLineSegment(sketch, "E286.MirrorCS", {"start": v(376.85, 287.2) * mm, "end": v(376.85, 295.4) * mm});
            skLineSegment(sketch, "E287.MirrorCS", {"start": v(376.85, 314.2) * mm, "end": v(380.05, 314.2) * mm});
            skLineSegment(sketch, "E288.MirrorCS", {"start": v(378.45, 300.7) * mm, "end": v(378.45, 319.5) * mm, "construction": true});
            skLineSegment(sketch, "E289.MirrorCS", {"start": v(376.85, 314.2) * mm, "end": v(376.85, 306) * mm});
            skLineSegment(sketch, "E290.MirrorCS", {"start": v(380.05, 314.2) * mm, "end": v(380.05, 306) * mm});
            skCircle(sketch, "E291.MirrorC", {"center": v(417.55, 276) * mm, "radius": 1.6 * mm});
            skPoint(sketch, "E292.MirrorP", {"position": v(378.45, 295.4) * mm});
            skPoint(sketch, "E293.MirrorP", {"position": v(378.45, 306) * mm});
            skLineSegment(sketch, "E294.MirrorCS", {"start": v(378.45, 391.4) * mm, "end": v(376.85, 391.4) * mm, "construction": true});
            skLineSegment(sketch, "E295.MirrorCS", {"start": v(378.45, 391.4) * mm, "end": v(378.45, 410.2) * mm, "construction": true});
            skLineSegment(sketch, "E296.MirrorCS", {"start": v(378.45, 410.2) * mm, "end": v(376.85, 410.2) * mm, "construction": true});
            skLineSegment(sketch, "E297.MirrorCS", {"start": v(376.85, 396.7) * mm, "end": v(380.05, 396.7) * mm});
            skLineSegment(sketch, "E298.MirrorCS", {"start": v(376.85, 423.7) * mm, "end": v(380.05, 423.7) * mm});
            skLineSegment(sketch, "E299.MirrorCS", {"start": v(376.85, 386.1) * mm, "end": v(380.05, 386.1) * mm});
            skLineSegment(sketch, "E300.MirrorCS", {"start": v(376.85, 404.9) * mm, "end": v(380.05, 404.9) * mm});
            skLineSegment(sketch, "E301.MirrorCS", {"start": v(376.85, 377.9) * mm, "end": v(380.05, 377.9) * mm});
            skLineSegment(sketch, "E302.MirrorCS", {"start": v(376.85, 415.5) * mm, "end": v(380.05, 415.5) * mm});
            skPoint(sketch, "E303.MirrorP", {"position": v(378.45, 386.1) * mm});
            skLineSegment(sketch, "E304.MirrorCS", {"start": v(380.05, 404.9) * mm, "end": v(380.05, 396.7) * mm});
            skLineSegment(sketch, "E305.MirrorCS", {"start": v(376.85, 377.9) * mm, "end": v(376.85, 386.1) * mm});
            skPoint(sketch, "E306.MirrorP", {"position": v(378.45, 396.7) * mm});
            skPoint(sketch, "E307.MirrorP", {"position": v(378.45, 423.7) * mm});
            skCircle(sketch, "E308.MirrorC", {"center": v(378.45, 410.2) * mm, "radius": 1.6 * mm});
            skLineSegment(sketch, "E309.MirrorCS", {"start": v(380.05, 377.9) * mm, "end": v(380.05, 386.1) * mm});
            skLineSegment(sketch, "E310.MirrorCS", {"start": v(380.05, 415.5) * mm, "end": v(380.05, 423.7) * mm});
            skCircle(sketch, "E311.MirrorC", {"center": v(378.45, 391.4) * mm, "radius": 1.6 * mm});
            skLineSegment(sketch, "E312.MirrorCS", {"start": v(376.85, 415.5) * mm, "end": v(376.85, 423.7) * mm});
            skLineSegment(sketch, "E313.MirrorCS", {"start": v(376.85, 404.9) * mm, "end": v(376.85, 396.7) * mm});
            skSolve(sketch);
        }
        {
            var Q0;
            Q0=makeQuery(id+"F0.imprint","IMPRINT",FACE,{"disambiguationData":[TD([[makeQuery(id+"F0.imprint","IMPRINT",EDGE,{"derivedFrom":sQuery(id+"F0.wireOp",EDGE,"E0")}),-1.0]])]});
            extrude(context, id + "F1", {"entities" : qUnion([Q0]), "depth" : 3 * mm, "offsetDistance" : 25 * mm});
        }
    });
